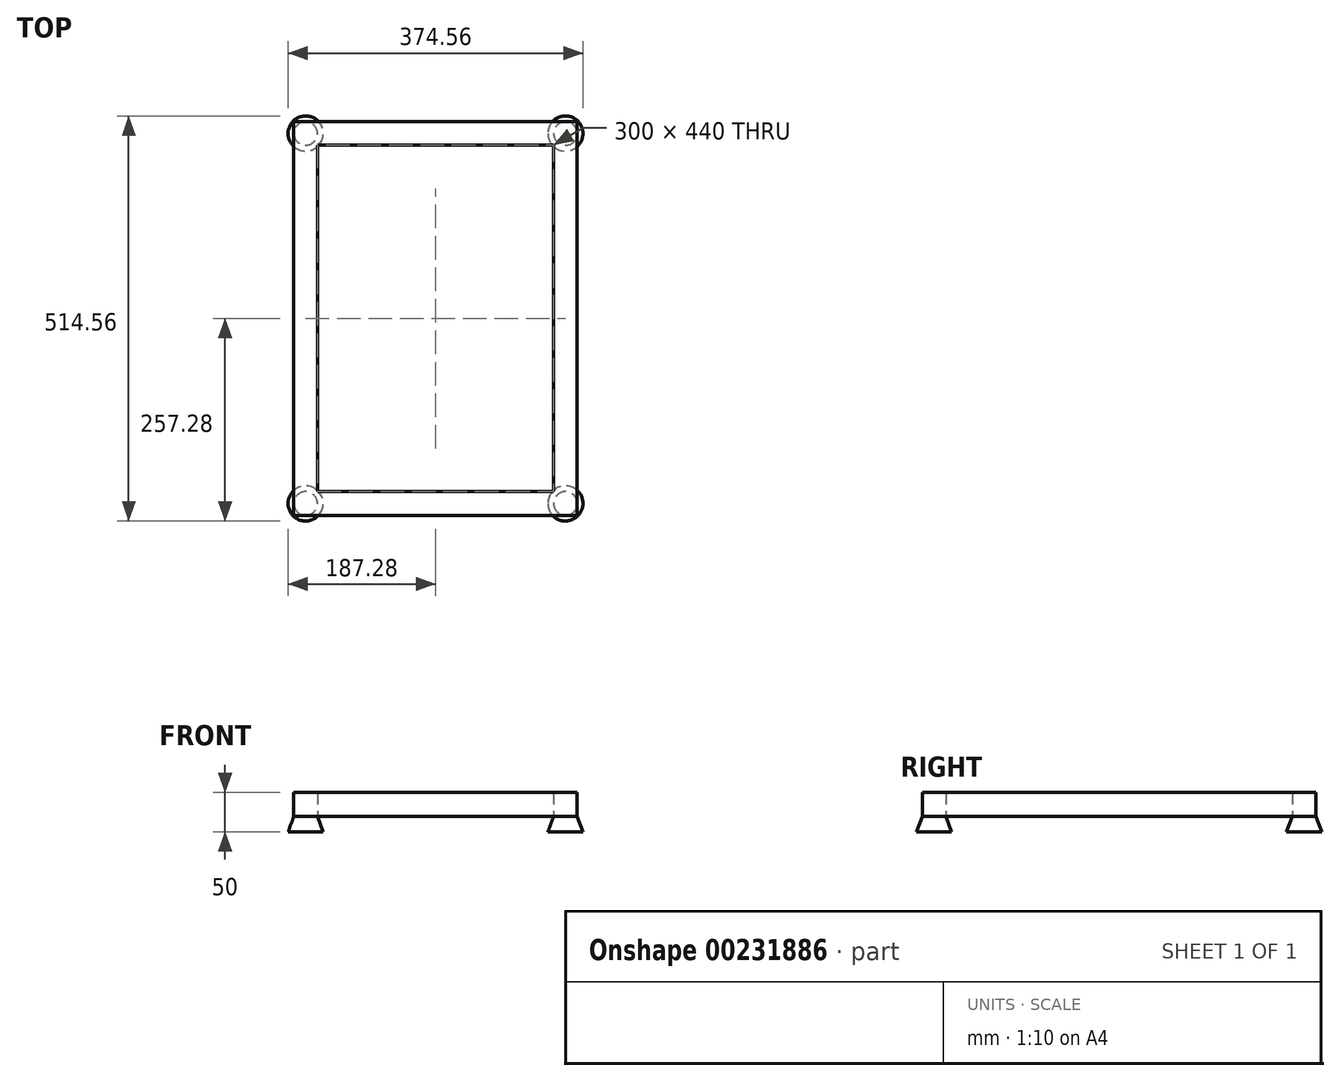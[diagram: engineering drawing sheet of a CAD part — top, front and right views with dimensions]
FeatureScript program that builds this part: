
annotation { "Feature Type Name" : "Feature", "Feature Type Description" : "" }
export const myFeature = defineFeature(function(context is Context, id is Id, definition is map)
    precondition{}
    {
        {
            var Q0;
            Q0=qCreatedBy(makeId("Top.planeOp"),FACE);
            var sketch = newSketch(context, id + "F0", { "sketchPlane" : qUnion([Q0])});
            skLineSegment(sketch, "E0.bottom", {"start": v(-180, 250) * mm, "end": v(180, 250) * mm});
            skLineSegment(sketch, "E0.top", {"start": v(-180, -250) * mm, "end": v(180, -250) * mm});
            skLineSegment(sketch, "E0.left", {"start": v(-180, 250) * mm, "end": v(-180, -250) * mm});
            skLineSegment(sketch, "E0.right", {"start": v(180, 250) * mm, "end": v(180, -250) * mm});
            skPoint(sketch, "E0.middle", {"position": v(0, 0) * mm});
            skLineSegment(sketch, "E1.0", {"start": v(-150, 220) * mm, "end": v(150, 220) * mm});
            skLineSegment(sketch, "E1.1", {"start": v(-150, 220) * mm, "end": v(-150, -220) * mm});
            skLineSegment(sketch, "E1.2", {"start": v(-150, -220) * mm, "end": v(150, -220) * mm});
            skLineSegment(sketch, "E1.3", {"start": v(150, 220) * mm, "end": v(150, -220) * mm});
            skSolve(sketch);
        }
        {
            var Q0;
            Q0 = qSketchRegion(id + "F0", true);
            extrude(context, id + "F1", {"entities" : qUnion([Q0]), "depth" : 30 * mm});
        }
        {
            var Q0;
            Q0=makeQuery(id+"F1.opExtrude","CAP_FACE",FACE,{"disambiguationData":[OSD([sQuery(id+"F0.wireOp",EDGE,"E0.bottom"),sQuery(id+"F0.wireOp",EDGE,"E0.top"),sQuery(id+"F0.wireOp",EDGE,"E0.left"),sQuery(id+"F0.wireOp",EDGE,"E0.right"),sQuery(id+"F0.wireOp",EDGE,"E1.0"),sQuery(id+"F0.wireOp",EDGE,"E1.1"),sQuery(id+"F0.wireOp",EDGE,"E1.2"),sQuery(id+"F0.wireOp",EDGE,"E1.3")])],"isStart":true});
            var sketch = newSketch(context, id + "F2", { "sketchPlane" : qUnion([Q0])});
            skCircle(sketch, "E2", {"center": v(-165, 235) * mm, "radius": 15 * mm});
            skCircle(sketch, "E3.0.1.0", {"center": v(-165, -235) * mm, "radius": 15 * mm});
            skCircle(sketch, "E3.1.0.0", {"center": v(165, 235) * mm, "radius": 15 * mm});
            skCircle(sketch, "E3.1.1.0", {"center": v(165, -235) * mm, "radius": 15 * mm});
            skLineSegment(sketch, "E3.direction1", {"start": v(-165, 235) * mm, "end": v(165, 235) * mm, "construction": true});
            skLineSegment(sketch, "E3.direction2", {"start": v(-165, 235) * mm, "end": v(-165, -235) * mm, "construction": true});
            skSolve(sketch);
        }
        {
            var Q0;
            Q0 = qSketchRegion(id + "F2", true);
            extrude(context, id + "F3", {"entities" : qUnion([Q0]), "operationType" : NewBodyOperationType.ADD, "depth" : 20 * mm, "hasDraft" : true, "draftAngle" : 20 * degree});
        }
    });
